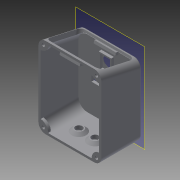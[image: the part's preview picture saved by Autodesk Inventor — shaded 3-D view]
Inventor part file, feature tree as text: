
AUTODESK INVENTOR PART (.ipt)
format: ipt  version: 2014 (Build 180170000, 170)  size: 430,080 bytes
history: native  units: mm
features: sketch x15, extrude x11, fillet x6, chamfer x3, loft x2, plane x1, projected_geometry x1
ambient origin geometry x8: Origin, YZ Plane, XZ Plane, XY Plane, X Axis, Y Axis, Z Axis, Center Point
bodies: Solid1 (feature_tree)
feature tree (39):
  sketch  "Sketch1"  dims[d0=70.0mm d1=90.0mm]
  plane  "Work Plane1"
  loft  "Loft1"
  sketch  "Sketch3"  dims[d6=0.0mm d7=90.0deg d8=60.0mm]
  sketch  "Sketch4"  dims[d9=40.0mm d10=65.0mm d11=85.0mm d12=65.0mm]
  sketch  "Sketch5"  dims[d13=75.0mm d14=5.0mm d15=0.0mm d16=5.0mm]
  extrude  "Extrusion1"  Depth=80.0mm
  fillet  "Fillet1"  [1 undecoded]
  loft  "Loft2"
  extrude  "Extrusion2"  Depth=65.0mm
  fillet  "Fillet2"  Radius=85.0mm
  fillet  "Fillet3"  Radius=65.0mm
  extrude  "Extrusion3"  Depth=75.0mm TaperAngle=0.0deg
  fillet  "Fillet4"  Radius=5.0mm
  extrude  "Extrusion4"  TaperAngle=0.0deg  [1 undecoded]
  extrude  "Extrusion5"  Depth=8.0mm
  extrude  "Extrusion6"  Depth=3.0mm TaperAngle=0.0deg
  chamfer  "Chamfer1"  Distance=3.0mm
  fillet  "Fillet5"  Radius=11.0mm
  extrude  "Extrusion7"  Depth=11.0mm
  extrude  "Extrusion8"  Depth=15.0mm
  chamfer  "Chamfer2"  Distance=3.0mm
  extrude  "Extrusion10"  Depth=3.0mm TaperAngle=0.0deg
  extrude  "Extrusion11"  Depth=15.0mm
  fillet  "Fillet6"  Radius=3.0mm
  extrude  "Extrusion12"  Depth=3.0mm
  chamfer  "Chamfer3"  Distance=18.0mm
  sketch  "Sketch2"  dims[d2=45.0mm d3=80.0mm d4=0.0mm d5=90.0deg]
  sketch  "Sketch6"  dims[d17=0.0mm d18=90.0deg d19=0.0mm d20=90.0deg]
  sketch  "Sketch7"  dims[d21=3.0mm d22=0.0mm d23=8.0mm]
  projected_geometry  "Projected Loop1"
  sketch  "Sketch8"  dims[d24=10.0mm d25=3.0mm d26=0.0mm]
  sketch  "Sketch9"  dims[d27=2.0mm]
  sketch  "Sketch10"  dims[d28=9.5mm d29=3.0mm d30=0.0mm d31=11.0mm]
  sketch  "Sketch11"  dims[d32=6.0mm d33=11.0mm]
  sketch  "Sketch12"  dims[d34=6.0mm d35=15.0mm]
  sketch  "Sketch14"  dims[d36=15.0mm]
  sketch  "Sketch15"  dims[d37=37.280029mm d38=3.0mm d39=0.0mm]
  sketch  "Sketch16"  dims[d40=10.0mm d41=3.0mm d42=0.0mm d43=15.0mm d44=3.0mm d45=2.0mm d46=45.0deg d47=3.0mm d48=18.0mm d49=18.0mm d50=18.0mm d51=18.0mm d52=3.0mm d53=0.0mm d54=2.5mm d55=2.5mm d56=2.5mm d57=2.5mm d58=3.0mm d59=0.0mm d60=0.5mm d61=2.0mm d62=45.0deg d69=11.0mm d70=13.0mm d71=2.0mm d72=1.5mm d73=1.5mm d74=1.5mm d75=1.5mm d76=3.0mm d77=0.0mm d78=7.5mm d79=7.5mm d80=19.0mm d81=19.0mm d82=18.0mm d83=18.0mm d84=3.0mm d85=0.0mm d86=2.0mm d87=10.0mm d88=10.0mm d89=3.0mm d90=0.0mm d91=3.0mm d92=2.0mm d93=45.0deg]
note: 2 required parameter values undecoded (feature->parameter linkage not recoverable at this tier; creation-order binding heuristic only, values carry confidence <= 0.55)
